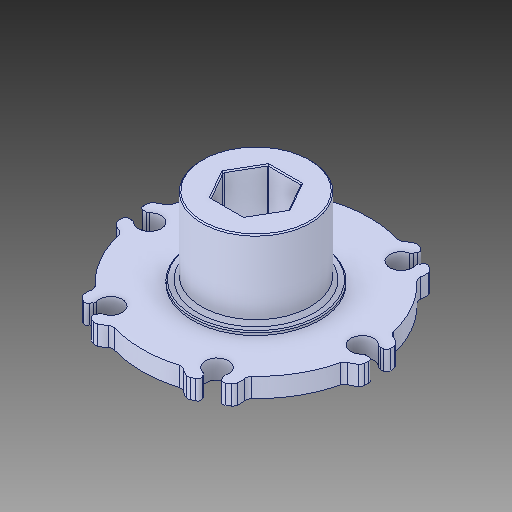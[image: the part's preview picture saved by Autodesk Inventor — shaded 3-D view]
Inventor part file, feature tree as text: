
AUTODESK INVENTOR PART (.ipt)
format: ipt  version: 2018 (Build 220112000, 112)  size: 285,184 bytes
history: native  units: in
note: dims shown in document units (in); Inventor stores cm internally (conversion verified against a paired STEP export)
features: fillet x1
ambient origin geometry x8: Origin, YZ Plane, XZ Plane, XY Plane, X Axis, Y Axis, Z Axis, Center Point
bodies: Solid1 (feature_tree)
feature tree (1):
  fillet  "Fillet7"  [1 undecoded]
note: 1 required parameter value undecoded (feature->parameter linkage not recoverable at this tier; creation-order binding heuristic only, values carry confidence <= 0.55)
